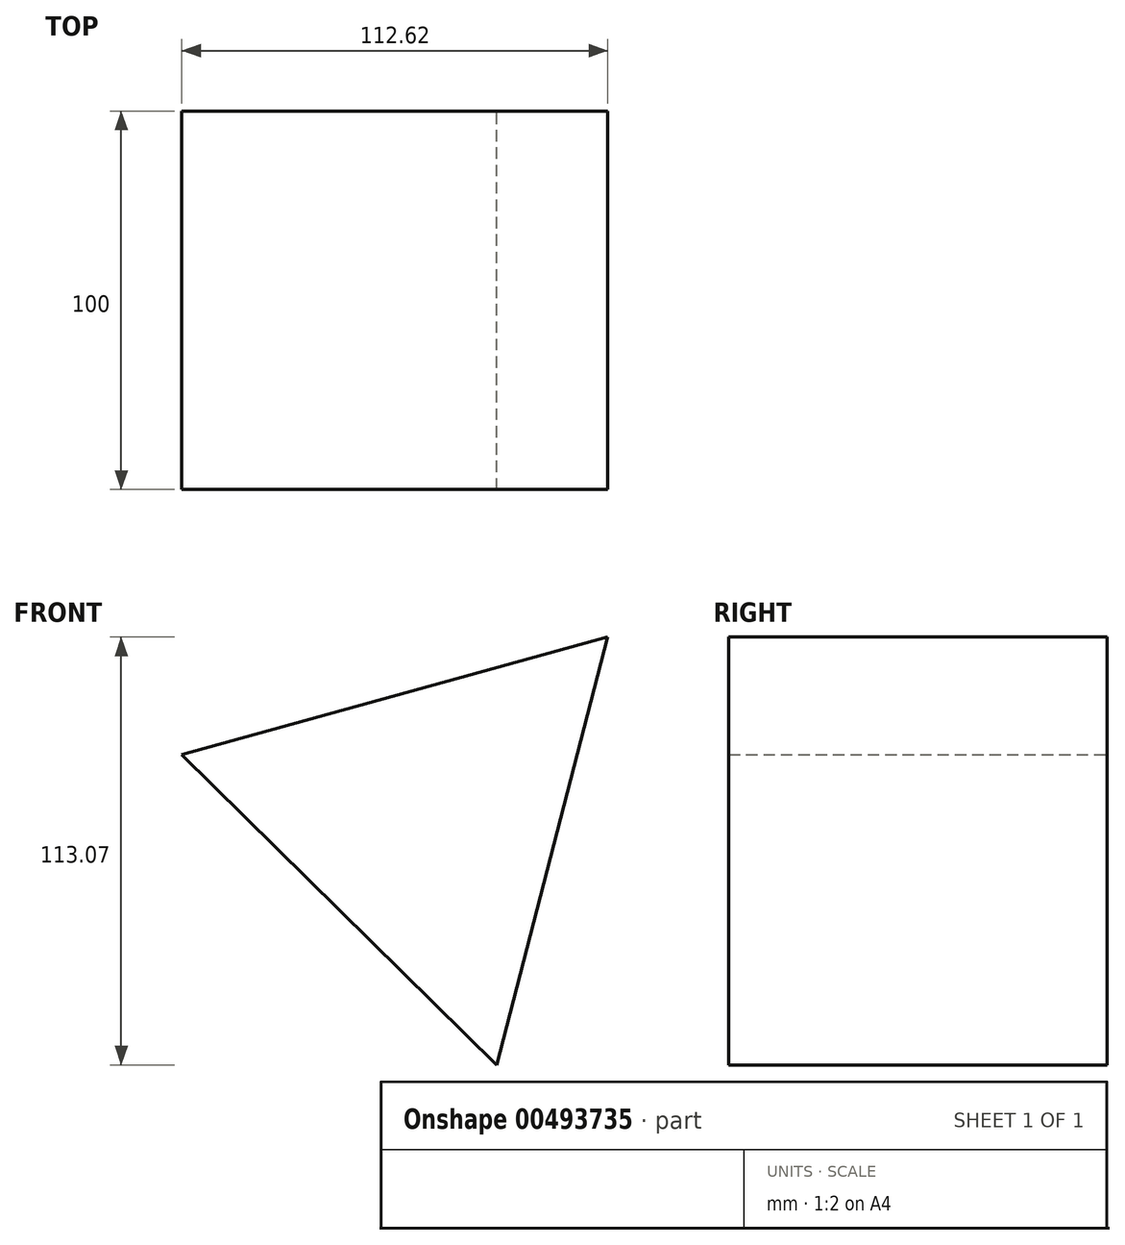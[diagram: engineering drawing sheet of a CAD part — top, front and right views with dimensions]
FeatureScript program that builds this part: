
annotation { "Feature Type Name" : "Feature", "Feature Type Description" : "" }
export const myFeature = defineFeature(function(context is Context, id is Id, definition is map)
    precondition{}
    {
        {
            var Q0;
            Q0=qCreatedBy(makeId("Front.planeOp"),FACE);
            var sketch = newSketch(context, id + "F0", { "sketchPlane" : qUnion([Q0])});
            skCircle(sketch, "E0.cCircle", {"center": v(0, 0) * mm, "radius": 67.45 * mm, "construction": true});
            skLineSegment(sketch, "E0.0", {"start": v(47.34, 48.05) * mm, "end": v(17.95, -65.02) * mm});
            skLineSegment(sketch, "E0.1", {"start": v(17.95, -65.02) * mm, "end": v(-65.28, 16.97) * mm});
            skLineSegment(sketch, "E0.2", {"start": v(-65.28, 16.97) * mm, "end": v(47.34, 48.05) * mm});
            skSolve(sketch);
        }
        {
            var Q0;
            Q0=makeQuery(id+"F0.imprint","IMPRINT",FACE,{"disambiguationData":[TD([[makeQuery(id+"F0.imprint","IMPRINT",EDGE,{"derivedFrom":sQuery(id+"F0.wireOp",EDGE,"E0.0")}),-1.0]])]});
            extrude(context, id + "F1", {"entities" : qUnion([Q0]), "depth" : 100 * mm});
        }
    });
